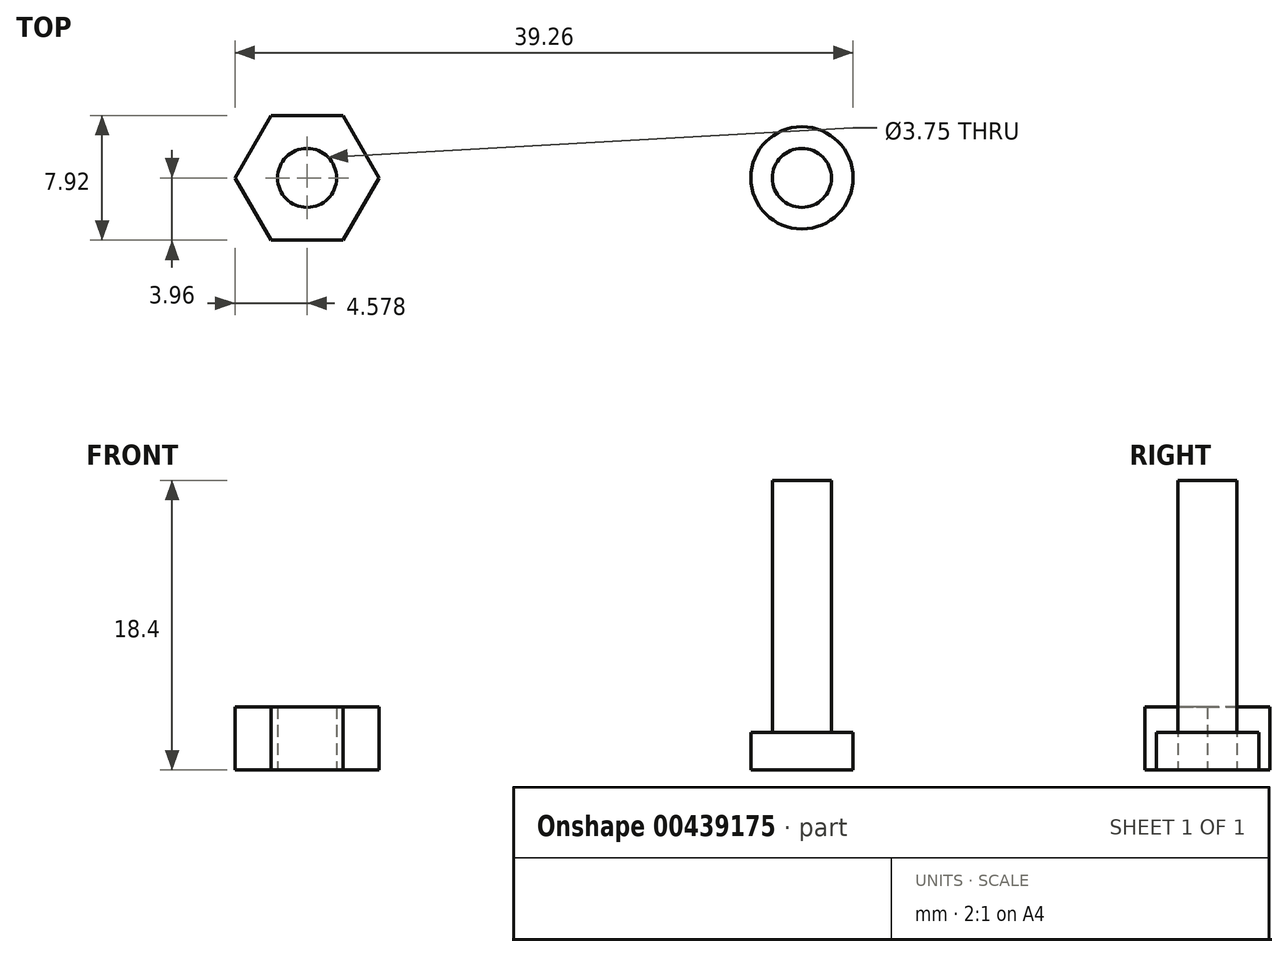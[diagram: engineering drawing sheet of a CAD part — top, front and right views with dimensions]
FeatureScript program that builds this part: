
annotation { "Feature Type Name" : "Feature", "Feature Type Description" : "" }
export const myFeature = defineFeature(function(context is Context, id is Id, definition is map)
    precondition{}
    {
        {
            var Q0;
            Q0=qCreatedBy(makeId("Top.planeOp"),FACE);
            var sketch = newSketch(context, id + "F0", { "sketchPlane" : qUnion([Q0])});
            skCircle(sketch, "E0", {"center": v(-14.9, 0) * mm, "radius": 1.88 * mm});
            skCircle(sketch, "E1.cCircle", {"center": v(-14.9, 0) * mm, "radius": 3.96 * mm, "construction": true});
            skLineSegment(sketch, "E1.0", {"start": v(-17.2, 3.97) * mm, "end": v(-12.61, 3.97) * mm});
            skLineSegment(sketch, "E1.1", {"start": v(-12.61, 3.97) * mm, "end": v(-10.32, 0) * mm});
            skLineSegment(sketch, "E1.2", {"start": v(-10.32, 0) * mm, "end": v(-12.61, -3.96) * mm});
            skLineSegment(sketch, "E1.3", {"start": v(-12.61, -3.97) * mm, "end": v(-17.2, -3.97) * mm});
            skLineSegment(sketch, "E1.4", {"start": v(-17.2, -3.97) * mm, "end": v(-19.48, 0) * mm});
            skLineSegment(sketch, "E1.5", {"start": v(-19.48, 0) * mm, "end": v(-17.2, 3.97) * mm});
            skPoint(sketch, "E1.0.midPoint", {"position": v(-14.9, 3.96) * mm});
            skSolve(sketch);
        }
        {
            var Q0;
            Q0 = qSketchRegion(id + "F0", true);
            extrude(context, id + "F1", {"entities" : qUnion([Q0]), "depth" : 4 * mm});
        }
        {
            var Q0;
            Q0=qCreatedBy(makeId("Top.planeOp"),FACE);
            var sketch = newSketch(context, id + "F2", { "sketchPlane" : qUnion([Q0])});
            skCircle(sketch, "E2", {"center": v(16.53, 0) * mm, "radius": 3.25 * mm});
            skSolve(sketch);
        }
        {
            var Q0;
            Q0 = qSketchRegion(id + "F2", true);
            extrude(context, id + "F3", {"entities" : qUnion([Q0]), "depth" : 2.4 * mm});
        }
        {
            var Q0;
            Q0=makeQuery(id+"F3.opExtrude","CAP_FACE",FACE,{"disambiguationData":[OSD([sQuery(id+"F2.wireOp",EDGE,"E2")])],"isStart":false});
            var sketch = newSketch(context, id + "F4", { "sketchPlane" : qUnion([Q0])});
            skCircle(sketch, "E3.0.0", {"center": v(16.53, 0) * mm, "radius": 3.25 * mm, "construction": true});
            skCircle(sketch, "E4", {"center": v(16.53, 0) * mm, "radius": 1.88 * mm});
            skSolve(sketch);
        }
        {
            var Q0;
            Q0 = qSketchRegion(id + "F4", true);
            extrude(context, id + "F5", {"entities" : qUnion([Q0]), "operationType" : NewBodyOperationType.ADD, "depth" : 16 * mm});
        }
    });
